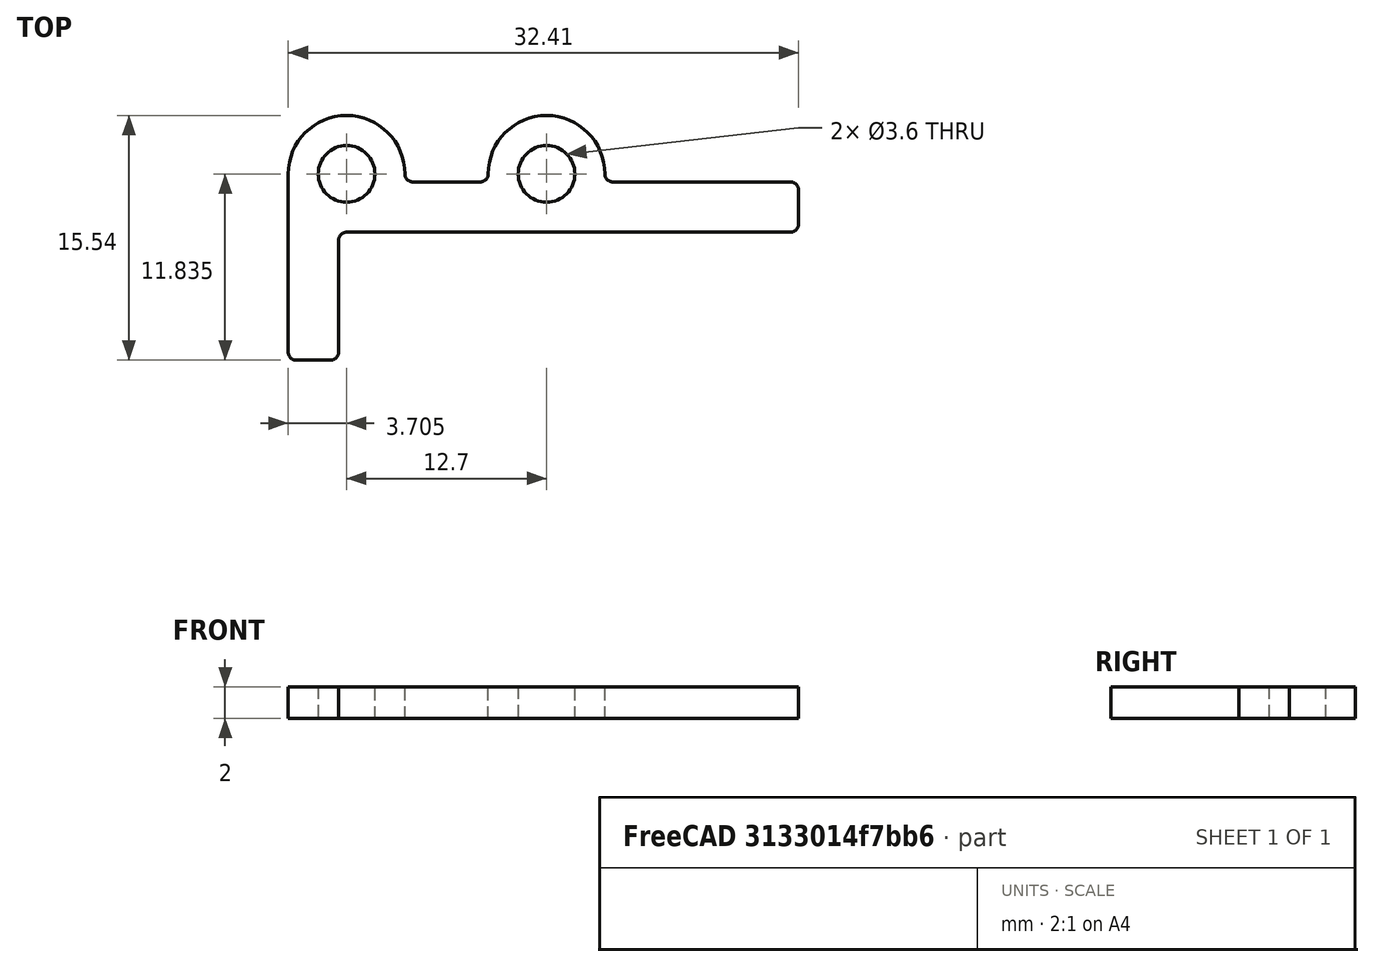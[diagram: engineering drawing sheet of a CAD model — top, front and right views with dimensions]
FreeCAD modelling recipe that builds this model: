
FCSTD DOCUMENT  (FreeCAD 0.22R38553 (Git))
Label: enclosure-panels
License: All rights reserved
LicenseURL: http://en.wikipedia.org/wiki/All_rights_reserved
objects: Sketcher::SketchObject×6, PartDesign::SubShapeBinder×1, PartDesign::Pad×1, PartDesign::Body×1
note: 17 computed .brp shape members not serialized (recipe doc carries the construction recipe); baked Part::Feature solids carry a one-line shape summary decoded from their .brp

FEATURE [Sketcher::SketchObject] Sketch  label="top"
  ArcFitTolerance = 1e-06
  FullyConstrained = true
  MakeInternals = false
  MapMode = 5
  expr: Constraints[23] = .Constraints.hole_distance
  sketch-geometry (14):
    g0: LineSegment StartX=-330.2 StartY=330.2 StartZ=0 EndX=-330.2 EndY=-330.2 EndZ=0
    g1: LineSegment StartX=-330.2 StartY=-330.2 StartZ=0 EndX=330.2 EndY=-330.2 EndZ=0
    g2: LineSegment StartX=330.2 StartY=-330.2 StartZ=0 EndX=330.2 EndY=330.2 EndZ=0
    g3: LineSegment StartX=330.2 StartY=330.2 StartZ=0 EndX=-330.2 EndY=330.2 EndZ=0
    g4: Circle CenterX=-292.1 CenterY=165.1 CenterZ=0 NormalX=0 NormalY=0 NormalZ=1 AngleXU=0 Radius=3.683
    g5: Circle CenterX=-292.1 CenterY=0 CenterZ=0 NormalX=0 NormalY=0 NormalZ=1 AngleXU=0 Radius=3.683
    g6: Circle CenterX=-292.1 CenterY=-165.1 CenterZ=0 NormalX=0 NormalY=0 NormalZ=1 AngleXU=0 Radius=3.683
    g7: Circle CenterX=292.1 CenterY=165.1 CenterZ=0 NormalX=0 NormalY=0 NormalZ=1 AngleXU=0 Radius=3.683
    g8: Circle CenterX=292.1 CenterY=0 CenterZ=0 NormalX=0 NormalY=0 NormalZ=1 AngleXU=0 Radius=3.683
    g9: Circle CenterX=292.1 CenterY=-165.1 CenterZ=0 NormalX=0 NormalY=0 NormalZ=1 AngleXU=0 Radius=3.683
    g10: LineSegment StartX=355.6 StartY=330.2 StartZ=0 EndX=355.6 EndY=320.2 EndZ=0
    g11: LineSegment StartX=355.6 StartY=320.2 StartZ=0 EndX=365.6 EndY=320.2 EndZ=0
    g12: LineSegment StartX=365.6 StartY=320.2 StartZ=0 EndX=365.6 EndY=330.2 EndZ=0
    g13: LineSegment StartX=365.6 StartY=330.2 StartZ=0 EndX=355.6 EndY=330.2 EndZ=0
  constraints (39):
    c: Coincident(g0,g1)
    c: Coincident(g1,g2)
    c: Coincident(g2,g3)
    c: Coincident(g3,g0)
    c: Vertical(g0)
    c: Vertical(g2)
    c: Horizontal(g1)
    c: Horizontal(g3)
    c: DistanceX(g3,g3) = 660.4
    c: DistanceY(g0,g0) = 660.4
    c: Symmetric(g0,g1,g-1)
    c: Diameter(g4) = 7.366
    c: DistanceX(g0,g4) = 38.1  'hole_distance'
    c: PointOnObject(g5,g-1)
    c: Equal(g4,g5)
    c: Equal(g4,g6)
    c: Vertical(g4,g5)
    c: Symmetric(g4,g6,g5)
    c: DistanceY(g4,g0) = 165.1
    c: Diameter(g7) = 7.366
    c: Equal(g7,g8)
    c: Equal(g7,g9)
    c: Symmetric(g7,g9,g8)
    c: DistanceX(g7,g2) = 38.1
    c: PointOnObject(g8,g-1)
    c: Horizontal(g4,g7)
    c: Vertical(g7,g8)
    c: Coincident(g10,g11)
    c: Coincident(g11,g12)
    c: Coincident(g12,g13)
    c: Coincident(g13,g10)
    c: Vertical(g10)
    c: Vertical(g12)
    c: Horizontal(g11)
    c: Horizontal(g13)
    c: Equal(g13,g10)
    c: Horizontal(g2,g10)
    c: Distance(g13,g13) = 10
    c: DistanceX(g2,g10) = 25.4
FEATURE [Sketcher::SketchObject] Sketch001  label="side"
  ArcFitTolerance = 1e-06
  FullyConstrained = true
  MakeInternals = false
  MapMode = 5
  expr: Constraints[23] = .Constraints.hole_distance
  sketch-geometry (22):
    g0: LineSegment StartX=-330.2 StartY=330.2 StartZ=0 EndX=-330.2 EndY=-330.2 EndZ=0
    g1: LineSegment StartX=-330.2 StartY=-330.2 StartZ=0 EndX=330.2 EndY=-330.2 EndZ=0
    g2: LineSegment StartX=330.2 StartY=-330.2 StartZ=0 EndX=330.2 EndY=330.2 EndZ=0
    g3: LineSegment StartX=330.2 StartY=330.2 StartZ=0 EndX=-330.2 EndY=330.2 EndZ=0
    g4: Circle CenterX=-292.1 CenterY=165.1 CenterZ=0 NormalX=0 NormalY=0 NormalZ=1 AngleXU=0 Radius=3.683
    g5: Circle CenterX=-292.1 CenterY=0 CenterZ=0 NormalX=0 NormalY=0 NormalZ=1 AngleXU=0 Radius=3.683
    g6: Circle CenterX=-292.1 CenterY=-165.1 CenterZ=0 NormalX=0 NormalY=0 NormalZ=1 AngleXU=0 Radius=3.683
    g7: Circle CenterX=292.1 CenterY=165.1 CenterZ=0 NormalX=0 NormalY=0 NormalZ=1 AngleXU=0 Radius=3.683
    g8: Circle CenterX=292.1 CenterY=0 CenterZ=0 NormalX=0 NormalY=0 NormalZ=1 AngleXU=0 Radius=3.683
    g9: Circle CenterX=292.1 CenterY=-165.1 CenterZ=0 NormalX=0 NormalY=0 NormalZ=1 AngleXU=0 Radius=3.683
    g10: LineSegment StartX=355.6 StartY=330.2 StartZ=0 EndX=355.6 EndY=320.2 EndZ=0
    g11: LineSegment StartX=355.6 StartY=320.2 StartZ=0 EndX=365.6 EndY=320.2 EndZ=0
    g12: LineSegment StartX=365.6 StartY=320.2 StartZ=0 EndX=365.6 EndY=330.2 EndZ=0
    g13: LineSegment StartX=365.6 StartY=330.2 StartZ=0 EndX=355.6 EndY=330.2 EndZ=0
    g14: Circle CenterX=177.8 CenterY=177.8 CenterZ=0 NormalX=0 NormalY=0 NormalZ=1 AngleXU=0 Radius=42.375
    g15: Circle CenterX=177.8 CenterY=126.8 CenterZ=0 NormalX=0 NormalY=0 NormalZ=1 AngleXU=0 Radius=1.8034
    g16: Circle CenterX=221.967 CenterY=203.3 CenterZ=0 NormalX=0 NormalY=0 NormalZ=1 AngleXU=0 Radius=1.8034
    g17: Circle CenterX=133.633 CenterY=203.3 CenterZ=0 NormalX=0 NormalY=0 NormalZ=1 AngleXU=0 Radius=1.8034
    g18: LineSegment [constr] StartX=177.8 StartY=177.8 StartZ=0 EndX=177.8 EndY=126.8 EndZ=0
    g19: LineSegment [constr] StartX=177.8 StartY=177.8 StartZ=0 EndX=221.967 EndY=203.3 EndZ=0
    g20: LineSegment [constr] StartX=177.8 StartY=177.8 StartZ=0 EndX=133.633 EndY=203.3 EndZ=0
    g21: Circle CenterX=-177.8 CenterY=-1.89e-14 CenterZ=0 NormalX=0 NormalY=0 NormalZ=1 AngleXU=0 Radius=4.5085
  constraints (62):
    c: Coincident(g0,g1)
    c: Coincident(g1,g2)
    c: Coincident(g2,g3)
    c: Coincident(g3,g0)
    c: Vertical(g0)
    c: Vertical(g2)
    c: Horizontal(g1)
    c: Horizontal(g3)
    c: DistanceX(g3,g3) = 660.4
    c: DistanceY(g0,g0) = 660.4
    c: Symmetric(g0,g1,g-1)
    c: Diameter(g4) = 7.366
    c: DistanceX(g0,g4) = 38.1  'hole_distance'
    c: PointOnObject(g5,g-1)
    c: Equal(g4,g5)
    c: Equal(g4,g6)
    c: Vertical(g4,g5)
    c: Symmetric(g4,g6,g5)
    c: DistanceY(g4,g0) = 165.1
    c: Diameter(g7) = 7.366
    c: Equal(g7,g8)
    c: Equal(g7,g9)
    c: Symmetric(g7,g9,g8)
    c: DistanceX(g7,g2) = 38.1
    c: PointOnObject(g8,g-1)
    c: Horizontal(g4,g7)
    c: Vertical(g7,g8)
    c: Coincident(g10,g11)
    c: Coincident(g11,g12)
    c: Coincident(g12,g13)
    c: Coincident(g13,g10)
    c: Vertical(g10)
    c: Vertical(g12)
    c: Horizontal(g11)
    c: Horizontal(g13)
    c: Equal(g13,g10)
    c: Horizontal(g2,g10)
    c: Distance(g13,g13) = 10
    c: DistanceX(g2,g10) = 25.4
    c: Diameter(g14) = 84.75
    c: Diameter(g15) = 3.6068
    c: Vertical(g14,g15)
    c: Equal(g15,g16)
    c: Equal(g15,g17)
    c: Coincident(g18,g14)
    c: Coincident(g18,g15)
    c: Coincident(g19,g14)
    c: Coincident(g19,g16)
    c: Coincident(g20,g14)
    c: Coincident(g20,g17)
    c: Equal(g18,g19)
    c: Equal(g18,g20)
    c: Distance(g15,g16) = 88.3346
    c: DistanceY(g14,g2) = 152.4
    c: Distance(g14,g2) = 152.4
    c: Diameter(g21) = 9.017
    c: DistanceX(g0,g21) = 152.4
    c: DistanceY(g0,g21) = 330.2
    c: DistanceY(g18,g18) = 51
    c: Angle(g20,g18) = 2.0944
    c: Angle(g18,g19) = 2.0944
    c: Diameter(g14) = 84.75
FEATURE [Sketcher::SketchObject] Sketch002  label="back"
  ArcFitTolerance = 1e-06
  FullyConstrained = true
  MakeInternals = false
  MapMode = 5
  expr: Constraints[23] = .Constraints.hole_distance
  sketch-geometry (23):
    g0: LineSegment StartX=-330.2 StartY=330.2 StartZ=0 EndX=-330.2 EndY=-330.2 EndZ=0
    g1: LineSegment StartX=-330.2 StartY=-330.2 StartZ=0 EndX=330.2 EndY=-330.2 EndZ=0
    g2: LineSegment StartX=330.2 StartY=-330.2 StartZ=0 EndX=330.2 EndY=330.2 EndZ=0
    g3: LineSegment StartX=330.2 StartY=330.2 StartZ=0 EndX=-330.2 EndY=330.2 EndZ=0
    g4: Circle CenterX=-292.1 CenterY=165.1 CenterZ=0 NormalX=0 NormalY=0 NormalZ=1 AngleXU=0 Radius=3.683
    g5: Circle CenterX=-292.1 CenterY=0 CenterZ=0 NormalX=0 NormalY=0 NormalZ=1 AngleXU=0 Radius=3.683
    g6: Circle CenterX=-292.1 CenterY=-165.1 CenterZ=0 NormalX=0 NormalY=0 NormalZ=1 AngleXU=0 Radius=3.683
    g7: Circle CenterX=292.1 CenterY=165.1 CenterZ=0 NormalX=0 NormalY=0 NormalZ=1 AngleXU=0 Radius=3.683
    g8: Circle CenterX=292.1 CenterY=0 CenterZ=0 NormalX=0 NormalY=0 NormalZ=1 AngleXU=0 Radius=3.683
    g9: Circle CenterX=292.1 CenterY=-165.1 CenterZ=0 NormalX=0 NormalY=0 NormalZ=1 AngleXU=0 Radius=3.683
    g10: LineSegment StartX=355.6 StartY=330.2 StartZ=0 EndX=355.6 EndY=320.2 EndZ=0
    g11: LineSegment StartX=355.6 StartY=320.2 StartZ=0 EndX=365.6 EndY=320.2 EndZ=0
    g12: LineSegment StartX=365.6 StartY=320.2 StartZ=0 EndX=365.6 EndY=330.2 EndZ=0
    g13: LineSegment StartX=365.6 StartY=330.2 StartZ=0 EndX=355.6 EndY=330.2 EndZ=0
    g14: Circle CenterX=-127 CenterY=-264.873 CenterZ=0 NormalX=0 NormalY=0 NormalZ=1 AngleXU=0 Radius=14.5274
    g15: Circle CenterX=-143 CenterY=-248.873 CenterZ=0 NormalX=0 NormalY=0 NormalZ=1 AngleXU=0 Radius=1.75
    g16: Circle CenterX=-111 CenterY=-248.873 CenterZ=0 NormalX=0 NormalY=0 NormalZ=1 AngleXU=0 Radius=1.75
    g17: Circle CenterX=-143 CenterY=-280.873 CenterZ=0 NormalX=0 NormalY=0 NormalZ=1 AngleXU=0 Radius=1.75
    g18: Circle CenterX=-111 CenterY=-280.873 CenterZ=0 NormalX=0 NormalY=0 NormalZ=1 AngleXU=0 Radius=1.75
    g19: LineSegment [constr] StartX=-127 StartY=-264.873 StartZ=0 EndX=-127 EndY=-279.4 EndZ=0
    g20: LineSegment [constr] StartX=-127 StartY=-264.873 StartZ=0 EndX=-111 EndY=-248.873 EndZ=0
    g21: GeomPoint [constr] X=-116.728 Y=-254.6 Z=0
    g22: GeomPoint [constr] X=-112.237 Y=-250.11 Z=0
  constraints (63):
    c: Coincident(g0,g1)
    c: Coincident(g1,g2)
    c: Coincident(g2,g3)
    c: Coincident(g3,g0)
    c: Vertical(g0)
    c: Vertical(g2)
    c: Horizontal(g1)
    c: Horizontal(g3)
    c: DistanceX(g3,g3) = 660.4
    c: DistanceY(g0,g0) = 660.4
    c: Symmetric(g0,g1,g-1)
    c: Diameter(g4) = 7.366
    c: DistanceX(g0,g4) = 38.1  'hole_distance'
    c: PointOnObject(g5,g-1)
    c: Equal(g4,g5)
    c: Equal(g4,g6)
    c: Vertical(g4,g5)
    c: Symmetric(g4,g6,g5)
    c: DistanceY(g4,g0) = 165.1
    c: Diameter(g7) = 7.366
    c: Equal(g7,g8)
    c: Equal(g7,g9)
    c: Symmetric(g7,g9,g8)
    c: DistanceX(g7,g2) = 38.1
    c: PointOnObject(g8,g-1)
    c: Horizontal(g4,g7)
    c: Vertical(g7,g8)
    c: Coincident(g10,g11)
    c: Coincident(g11,g12)
    c: Coincident(g12,g13)
    c: Coincident(g13,g10)
    c: Vertical(g10)
    c: Vertical(g12)
    c: Horizontal(g11)
    c: Horizontal(g13)
    c: Equal(g13,g10)
    c: Horizontal(g2,g10)
    c: Distance(g13,g13) = 10
    c: DistanceX(g2,g10) = 25.4
    c: Equal(g15,g16)
    c: Equal(g15,g17)
    c: Equal(g15,g18)
    c: DistanceY(g17,g15) = 31.9999
    c: DistanceX(g15,g16) = 31.9999
    c: Vertical(g15,g17)
    c: Vertical(g16,g18)
    c: Horizontal(g15,g16)
    c: Horizontal(g17,g18)
    c: Diameter(g15) = 3.49999
    c: Symmetric(g15,g18,g14)
    c: Coincident(g19,g14)
    c: PointOnObject(g19,g14)
    c: Vertical(g19)
    c: DistanceY(g0,g19) = 50.8
    c: DistanceX(g0,g14) = 203.2
    c: Coincident(g20,g14)
    c: Coincident(g20,g16)
    c: PointOnObject(g21,g14)
    c: PointOnObject(g21,g20)
    c: PointOnObject(g22,g16)
    c: PointOnObject(g22,g20)
    c: Distance(g21,g22) = 6.35
    c: Diameter(g14) = 29.0548
FEATURE [Sketcher::SketchObject] Sketch003  label="bottom"
  ArcFitTolerance = 1e-06
  FullyConstrained = true
  MakeInternals = false
  MapMode = 5
  expr: Constraints[66] = 1.53 "
  sketch-geometry (24):
    g0: LineSegment StartX=-328.93 StartY=271.526 StartZ=0 EndX=-328.93 EndY=-284.988 EndZ=0
    g1: LineSegment StartX=-302.768 StartY=-323.85 StartZ=0 EndX=302.768 EndY=-323.85 EndZ=0
    g2: LineSegment StartX=328.93 StartY=-284.988 StartZ=0 EndX=328.93 EndY=271.526 EndZ=0
    g3: LineSegment StartX=276.606 StartY=323.85 StartZ=0 EndX=-276.606 EndY=323.85 EndZ=0
    g4: LineSegment StartX=354.33 StartY=323.85 StartZ=0 EndX=354.33 EndY=313.85 EndZ=0
    g5: LineSegment StartX=354.33 StartY=313.85 StartZ=0 EndX=364.33 EndY=313.85 EndZ=0
    g6: LineSegment StartX=364.33 StartY=313.85 StartZ=0 EndX=364.33 EndY=323.85 EndZ=0
    g7: LineSegment StartX=364.33 StartY=323.85 StartZ=0 EndX=354.33 EndY=323.85 EndZ=0
    g8: GeomPoint [constr] X=-328.93 Y=323.85 Z=0
    g9: GeomPoint [constr] X=-328.93 Y=-323.85 Z=0
    g10: GeomPoint [constr] X=328.93 Y=-323.85 Z=0
    g11: GeomPoint [constr] X=328.93 Y=323.85 Z=0
    g12: LineSegment StartX=-328.93 StartY=271.526 StartZ=0 EndX=-302.768 EndY=271.526 EndZ=0
    g13: LineSegment StartX=-302.768 StartY=271.526 StartZ=0 EndX=-302.768 EndY=297.688 EndZ=0
    g14: LineSegment StartX=-302.768 StartY=297.688 StartZ=0 EndX=-276.606 EndY=297.688 EndZ=0
    g15: LineSegment StartX=-276.606 StartY=297.688 StartZ=0 EndX=-276.606 EndY=323.85 EndZ=0
    g16: LineSegment StartX=276.606 StartY=323.85 StartZ=0 EndX=276.606 EndY=297.688 EndZ=0
    g17: LineSegment StartX=276.606 StartY=297.688 StartZ=0 EndX=302.768 EndY=297.688 EndZ=0
    g18: LineSegment StartX=302.768 StartY=297.688 StartZ=0 EndX=302.768 EndY=271.526 EndZ=0
    g19: LineSegment StartX=302.768 StartY=271.526 StartZ=0 EndX=328.93 EndY=271.526 EndZ=0
    g20: LineSegment StartX=-328.93 StartY=-284.988 StartZ=0 EndX=-302.768 EndY=-284.988 EndZ=0
    g21: LineSegment StartX=-302.768 StartY=-284.988 StartZ=0 EndX=-302.768 EndY=-323.85 EndZ=0
    g22: LineSegment StartX=302.768 StartY=-323.85 StartZ=0 EndX=302.768 EndY=-284.988 EndZ=0
    g23: LineSegment StartX=302.768 StartY=-284.988 StartZ=0 EndX=328.93 EndY=-284.988 EndZ=0
  constraints (64):
    c: Vertical(g0)
    c: Vertical(g2)
    c: Horizontal(g1)
    c: Horizontal(g3)
    c: DistanceX(g8,g11) = 657.86
    c: DistanceY(g9,g8) = 647.7
    c: Symmetric(g8,g10,g-1)
    c: Coincident(g4,g5)
    c: Coincident(g5,g6)
    c: Coincident(g6,g7)
    c: Coincident(g7,g4)
    c: Vertical(g4)
    c: Vertical(g6)
    c: Horizontal(g5)
    c: Horizontal(g7)
    c: Equal(g7,g4)
    c: Horizontal(g11,g4)
    c: Distance(g7,g7) = 10
    c: DistanceX(g11,g4) = 25.4
    c: PointOnObject(g8,g0)
    c: PointOnObject(g8,g3)
    c: PointOnObject(g9,g0)
    c: PointOnObject(g9,g1)
    c: PointOnObject(g10,g1)
    c: PointOnObject(g10,g2)
    c: PointOnObject(g11,g2)
    c: PointOnObject(g11,g3)
    c: Coincident(g12,g0)
    c: Horizontal(g12)
    c: Coincident(g13,g12)
    c: Vertical(g13)
    c: Coincident(g14,g13)
    c: Horizontal(g14)
    c: Coincident(g15,g14)
    c: Coincident(g15,g3)
    c: Vertical(g15)
    c: Coincident(g3,g16)
    c: Coincident(g16,g17)
    c: Horizontal(g17)
    c: Coincident(g17,g18)
    c: Vertical(g18)
    c: Coincident(g18,g19)
    c: Coincident(g19,g2)
    c: Horizontal(g19)
    c: Vertical(g16)
    c: Equal(g12, g13-g16) x4
    c: Equal(g16,g17)
    c: Equal(g17,g18)
    c: Equal(g18,g19)
    c: Coincident(g0,g20)
    c: Horizontal(g20)
    c: Coincident(g20,g21)
    c: Coincident(g21,g1)
    c: Vertical(g21)
    c: Coincident(g1,g22)
    c: Vertical(g22)
    c: Coincident(g22,g23)
    c: Coincident(g23,g2)
    c: Horizontal(g23)
    c: Equal(g21,g22)
    c: Equal(g12,g20)
    c: Equal(g19,g23)
    c: Distance(g12,g12) = 26.162  'bracket_width'
    c: Distance(g21,g21) = 38.862
FEATURE [Sketcher::SketchObject] Sketch004  label="door"
  ArcFitTolerance = 1e-06
  FullyConstrained = true
  MakeInternals = false
  MapMode = 5
  expr: Constraints[36] = .Constraints.hinge_dist
  expr: Constraints[58] = .Constraints.door_stop_gap
  expr: Constraints[94] = .Constraints.door_stop_gap
  expr: Constraints[95] = .Constraints.door_stop_gap
  sketch-geometry (36):
    g0: LineSegment StartX=-151.765 StartY=304.038 StartZ=0 EndX=-151.765 EndY=-304.038 EndZ=0
    g1: LineSegment StartX=-151.765 StartY=-304.038 StartZ=0 EndX=151.765 EndY=-304.038 EndZ=0
    g2: LineSegment StartX=151.765 StartY=-304.038 StartZ=0 EndX=151.765 EndY=304.038 EndZ=0
    g3: LineSegment StartX=151.765 StartY=304.038 StartZ=0 EndX=-151.765 EndY=304.038 EndZ=0
    g4: LineSegment StartX=177.165 StartY=304.038 StartZ=0 EndX=177.165 EndY=314.038 EndZ=0
    g5: LineSegment StartX=177.165 StartY=314.038 StartZ=0 EndX=187.165 EndY=314.038 EndZ=0
    g6: LineSegment StartX=187.165 StartY=314.038 StartZ=0 EndX=187.165 EndY=304.038 EndZ=0
    g7: LineSegment StartX=187.165 StartY=304.038 StartZ=0 EndX=177.165 EndY=304.038 EndZ=0
    g8: Circle CenterX=107.823 CenterY=59.5 CenterZ=0 NormalX=0 NormalY=0 NormalZ=1 AngleXU=0 Radius=4.2545
    g9: Circle CenterX=107.823 CenterY=-59.5 CenterZ=0 NormalX=0 NormalY=0 NormalZ=1 AngleXU=0 Radius=4.2545
    g10: Circle CenterX=-135.255 CenterY=227.838 CenterZ=0 NormalX=0 NormalY=0 NormalZ=1 AngleXU=0 Radius=3.3782
    g11: Circle CenterX=-135.255 CenterY=199.847 CenterZ=0 NormalX=0 NormalY=0 NormalZ=1 AngleXU=0 Radius=3.3782
    g12: Circle CenterX=-135.255 CenterY=-199.847 CenterZ=0 NormalX=0 NormalY=0 NormalZ=1 AngleXU=0 Radius=3.3782
    g13: Circle CenterX=-135.255 CenterY=-227.838 CenterZ=0 NormalX=0 NormalY=0 NormalZ=1 AngleXU=0 Radius=3.3782
    g14: LineSegment [constr] StartX=-135.255 StartY=199.847 StartZ=0 EndX=-135.255 EndY=0 EndZ=0
    g15: LineSegment [constr] StartX=-135.255 StartY=-199.847 StartZ=0 EndX=-135.255 EndY=0 EndZ=0
    g16: LineSegment [constr] StartX=121.795 StartY=-302.768 StartZ=0 EndX=150.495 EndY=-302.768 EndZ=0
    g17: LineSegment [constr] StartX=150.495 StartY=-302.768 StartZ=0 EndX=150.495 EndY=-283.168 EndZ=0
    g18: LineSegment [constr] StartX=150.495 StartY=-283.168 StartZ=0 EndX=121.795 EndY=-283.168 EndZ=0
    g19: LineSegment [constr] StartX=121.795 StartY=-283.168 StartZ=0 EndX=121.795 EndY=-302.768 EndZ=0
    g20: Circle CenterX=136.145 CenterY=-292.968 CenterZ=0 NormalX=0 NormalY=0 NormalZ=1 AngleXU=0 Radius=2.75
    g21: Circle CenterX=134.495 CenterY=-278.955 CenterZ=0 NormalX=0 NormalY=0 NormalZ=1 AngleXU=0 Radius=1.8
    g22: Circle CenterX=121.795 CenterY=-278.955 CenterZ=0 NormalX=0 NormalY=0 NormalZ=1 AngleXU=0 Radius=1.8
    g23: LineSegment [constr] StartX=134.495 StartY=-278.955 StartZ=0 EndX=134.495 EndY=-280.755 EndZ=0
    g24: LineSegment [constr] StartX=134.495 StartY=-280.755 StartZ=0 EndX=134.495 EndY=-283.168 EndZ=0
    g25: LineSegment [constr] StartX=134.495 StartY=-278.955 StartZ=0 EndX=136.295 EndY=-278.955 EndZ=0
    g26: LineSegment [constr] StartX=121.795 StartY=302.768 StartZ=0 EndX=150.495 EndY=302.768 EndZ=0
    g27: LineSegment [constr] StartX=150.495 StartY=302.768 StartZ=0 EndX=150.495 EndY=283.168 EndZ=0
    g28: LineSegment [constr] StartX=150.495 StartY=283.168 StartZ=0 EndX=121.795 EndY=283.168 EndZ=0
    g29: LineSegment [constr] StartX=121.795 StartY=283.168 StartZ=0 EndX=121.795 EndY=302.768 EndZ=0
    g30: Circle CenterX=136.145 CenterY=292.968 CenterZ=0 NormalX=0 NormalY=0 NormalZ=1 AngleXU=0 Radius=2.75
    g31: Circle CenterX=134.495 CenterY=278.955 CenterZ=0 NormalX=0 NormalY=0 NormalZ=1 AngleXU=0 Radius=1.8
    g32: Circle CenterX=121.795 CenterY=278.955 CenterZ=0 NormalX=0 NormalY=0 NormalZ=1 AngleXU=0 Radius=1.8
    g33: LineSegment [constr] StartX=134.495 StartY=278.955 StartZ=0 EndX=134.495 EndY=280.755 EndZ=0
    g34: LineSegment [constr] StartX=134.495 StartY=280.755 StartZ=0 EndX=134.495 EndY=283.168 EndZ=0
    g35: LineSegment [constr] StartX=134.495 StartY=278.955 StartZ=0 EndX=136.295 EndY=278.955 EndZ=0
  constraints (103):
    c: Coincident(g0,g1)
    c: Coincident(g1,g2)
    c: Coincident(g2,g3)
    c: Coincident(g3,g0)
    c: Vertical(g0)
    c: Vertical(g2)
    c: Horizontal(g1)
    c: Horizontal(g3)
    c: DistanceX(g3,g3) = 303.53
    c: DistanceY(g0,g0) = 608.076
    c: Symmetric(g0,g1,g-1)
    c: Coincident(g4,g5)
    c: Coincident(g5,g6)
    c: Coincident(g6,g7)
    c: Coincident(g7,g4)
    c: Vertical(g4)
    c: Vertical(g6)
    c: Horizontal(g5)
    c: Horizontal(g7)
    c: Equal(g7,g4)
    c: Horizontal(g2,g4)
    c: Distance(g7,g7) = 10
    c: DistanceX(g2,g4) = 25.4
    c: Equal(g8,g9)
    c: Diameter(g8) = 8.509
    c: DistanceY(g9,g8) = 119
    c: Symmetric(g8,g9,g-1)
    c: DistanceX(g9,g1) = 43.942
    c: Equal(g10,g11)
    c: Equal(g10,g12)
    c: Equal(g10,g13)
    c: Diameter(g10) = 6.7564
    c: Vertical(g10,g11)
    c: Vertical(g10,g12)
    c: Vertical(g12,g13)
    c: DistanceY(g11,g10) = 27.9908  'hinge_dist'
    c: DistanceY(g13,g12) = 27.9908
    c: Coincident(g14,g11)
    c: PointOnObject(g14,g-1)
    c: Vertical(g14)
    c: Coincident(g15,g12)
    c: Coincident(g15,g14)
    c: Equal(g14,g15)
    c: DistanceX(g0,g10) = 16.51
    c: DistanceY(g10,g0) = 76.2
    c: Coincident(g16,g17)
    c: Coincident(g17,g18)
    c: Coincident(g18,g19)
    c: Coincident(g19,g16)
    c: Horizontal(g16)
    c: Horizontal(g18)
    c: Vertical(g17)
    c: Vertical(g19)
    c: DistanceX(g18,g18) = 28.7
    c: DistanceY(g19,g19) = 19.6
    c: Symmetric(g18,g16,g20)
    c: Diameter(g20) = 5.5
    c: Distance(g16,g2) = 1.27  'door_stop_gap'
    c: Distance(g16,g1) = 1.27
    c: Equal(g21,g22)
    c: Diameter(g21) = 3.6
    c: Coincident(g23,g21)
    c: PointOnObject(g23,g21)
    c: Vertical(g23)
    c: Coincident(g24,g23)
    c: PointOnObject(g24,g18)
    c: Vertical(g24)
    c: DistanceY(g24,g24) = 2.413
    c: Horizontal(g22,g21)
    c: DistanceX(g22,g21) = 12.7
    c: Coincident(g25,g21)
    c: PointOnObject(g25,g21)
    c: Horizontal(g25)
    c: Coincident(g26,g27)
    c: Coincident(g27,g28)
    c: Coincident(g28,g29)
    c: Coincident(g29,g26)
    c: Horizontal(g26)
    c: Horizontal(g28)
    c: Vertical(g27)
    c: Vertical(g29)
    c: Symmetric(g28,g26,g30)
    c: Diameter(g30) = 5.5
    c: Equal(g31,g32)
    c: Diameter(g31) = 3.6
    c: Coincident(g33,g31)
    c: PointOnObject(g33,g31)
    c: Vertical(g33)
    c: Coincident(g34,g33)
    c: PointOnObject(g34,g28)
    c: Vertical(g34)
    c: Coincident(g35,g31)
    c: PointOnObject(g35,g31)
    c: Horizontal(g35)
    c: DistanceY(g26,g2) = 1.27
    c: DistanceX(g26,g2) = 1.27
    c: Equal(g26,g18)
    c: Equal(g19,g29)
    c: Horizontal(g32,g31)
    c: DistanceY(g34,g34) = 2.413
    c: Vertical(g31,g21)
    c: Vertical(g22,g18)
    c: Vertical(g32,g22)
FEATURE [PartDesign::SubShapeBinder] Binder
  BindCopyOnChange = 0
  BindMode = 0
  ClaimChildren = false
  Context = -> Body [Binder.]
  Fuse = false
  MakeFace = true
  OffsetFill = false
  OffsetIntersection = false
  OffsetJoinType = 0
  OffsetOpenResult = false
  PartialLoad = false
  Relative = true
  Support = -> [Sketch004]
  _Version = 2
FEATURE [Sketcher::SketchObject] Sketch005  label="stops"
  ArcFitTolerance = 1e-06
  ExternalGeometry = -> [Binder]
  FullyConstrained = true
  MakeInternals = false
  MapMode = 5
  sketch-geometry (27):
    g0: LineSegment [constr] StartX=121.795 StartY=-302.768 StartZ=0 EndX=150.495 EndY=-302.768 EndZ=0
    g1: LineSegment [constr] StartX=150.495 StartY=-302.768 StartZ=0 EndX=150.495 EndY=-283.168 EndZ=0
    g2: LineSegment [constr] StartX=150.495 StartY=-283.168 StartZ=0 EndX=121.795 EndY=-283.168 EndZ=0
    g3: LineSegment [constr] StartX=121.795 StartY=-283.168 StartZ=0 EndX=121.795 EndY=-302.768 EndZ=0
    g4: Circle CenterX=121.795 CenterY=-278.955 CenterZ=0 NormalX=0 NormalY=0 NormalZ=1 AngleXU=0 Radius=1.8
    g5: LineSegment StartX=121.287 StartY=-283.168 StartZ=0 EndX=121.287 EndY=-290.28 EndZ=0
    g6: LineSegment StartX=120.779 StartY=-290.788 StartZ=0 EndX=118.598 EndY=-290.788 EndZ=0
    g7: LineSegment StartX=118.09 StartY=-290.28 StartZ=0 EndX=118.09 EndY=-278.955 EndZ=0
    g8: ArcOfCircle CenterX=121.795 CenterY=-283.168 CenterZ=0 NormalX=0 NormalY=0 NormalZ=1 AngleXU=0 Radius=0.508 StartAngle=1.5708 EndAngle=3.14159
    g9: ArcOfCircle CenterX=121.795 CenterY=-278.955 CenterZ=0 NormalX=0 NormalY=0 NormalZ=1 AngleXU=0 Radius=3.705 StartAngle=4.1e-15 EndAngle=3.14159
    g10: ArcOfCircle CenterX=126.008 CenterY=-278.955 CenterZ=0 NormalX=0 NormalY=0 NormalZ=1 AngleXU=0 Radius=0.508 StartAngle=3.14159 EndAngle=4.71239
    g11: LineSegment StartX=126.008 StartY=-279.463 StartZ=0 EndX=130.282 EndY=-279.463 EndZ=0
    g12: ArcOfCircle CenterX=130.282 CenterY=-278.955 CenterZ=0 NormalX=0 NormalY=0 NormalZ=1 AngleXU=0 Radius=0.508 StartAngle=4.71239 EndAngle=6.28319
    g13: ArcOfCircle CenterX=118.598 CenterY=-290.28 CenterZ=0 NormalX=0 NormalY=0 NormalZ=1 AngleXU=0 Radius=0.508 StartAngle=3.14159 EndAngle=4.71239
    g14: GeomPoint [constr] X=118.09 Y=-290.788 Z=0
    g15: ArcOfCircle CenterX=120.779 CenterY=-290.28 CenterZ=0 NormalX=0 NormalY=0 NormalZ=1 AngleXU=0 Radius=0.508 StartAngle=4.71239 EndAngle=6.28319
    g16: GeomPoint [constr] X=121.287 Y=-290.788 Z=0
    g17: ArcOfCircle CenterX=149.987 CenterY=-282.152 CenterZ=0 NormalX=0 NormalY=0 NormalZ=1 AngleXU=0 Radius=0.508 StartAngle=4.71239 EndAngle=6.28319
    g18: Circle CenterX=134.495 CenterY=-278.955 CenterZ=0 NormalX=0 NormalY=0 NormalZ=1 AngleXU=0 Radius=1.8
    g19: ArcOfCircle CenterX=134.495 CenterY=-278.955 CenterZ=0 NormalX=0 NormalY=0 NormalZ=1 AngleXU=0 Radius=3.705 StartAngle=5.9e-15 EndAngle=3.14159
    g20: ArcOfCircle CenterX=138.708 CenterY=-278.955 CenterZ=0 NormalX=0 NormalY=0 NormalZ=1 AngleXU=0 Radius=0.508 StartAngle=3.14159 EndAngle=4.71239
    g21: LineSegment StartX=138.708 StartY=-279.463 StartZ=0 EndX=149.987 EndY=-279.463 EndZ=0
    g22: ArcOfCircle CenterX=149.987 CenterY=-279.971 CenterZ=0 NormalX=0 NormalY=0 NormalZ=1 AngleXU=0 Radius=0.508 StartAngle=4.06e-14 EndAngle=1.5708
    g23: LineSegment StartX=150.495 StartY=-282.152 StartZ=0 EndX=150.495 EndY=-279.971 EndZ=0
    g24: LineSegment [constr] StartX=134.495 StartY=-278.955 StartZ=0 EndX=136.295 EndY=-278.955 EndZ=0
    g25: LineSegment [constr] StartX=136.295 StartY=-278.955 StartZ=0 EndX=138.2 EndY=-278.955 EndZ=0
    g26: LineSegment StartX=121.795 StartY=-282.66 StartZ=0 EndX=149.987 EndY=-282.66 EndZ=0
  constraints (65):
    c: Coincident(g0,g1)
    c: Coincident(g1,g2)
    c: Coincident(g2,g3)
    c: Coincident(g3,g0)
    c: Horizontal(g0)
    c: Horizontal(g2)
    c: Vertical(g1)
    c: Vertical(g3)
    c: DistanceX(g2,g2) = 28.7
    c: DistanceY(g3,g3) = 19.6
    c: Diameter(g4) = 3.6
    c: Vertical(g5)
    c: Horizontal(g6)
    c: Vertical(g7)
    c: Tangent(g5,g8) = -1.5708
    c: Tangent(g7,g9) = 1.5708
    c: Tangent(g9,g10) = 1.5708
    c: Tangent(g10,g11) = -1.5708
    c: Tangent(g11,g12) = -1.5708
    c: Horizontal(g11)
    c: Equal(g10,g12)
    c: PointOnObject(g14,g7)
    c: PointOnObject(g14,g6)
    c: Tangent(g7,g13) = 1.5708
    c: Tangent(g6,g13) = 1.5708
    c: PointOnObject(g16,g6)
    c: PointOnObject(g16,g5)
    c: Tangent(g6,g15) = 1.5708
    c: Tangent(g5,g15) = 1.5708
    c: Equal(g10,g8)
    c: Equal(g10,g15)
    c: Equal(g10,g13)
    c: Horizontal(g10,g9)
    c: Coincident(g8,g2)
    c: DistanceY(g6,g2) = 7.62
    c: Symmetric(g2,g0,g-3)
    c: Coincident(g9,g4)
    c: Equal(g17,g12)
    c: Coincident(g4,g-5)
    c: Tangent(g12,g19) = 1.5708
    c: Tangent(g19,g20) = 1.5708
    c: Tangent(g20,g21) = -1.5708
    c: Tangent(g21,g22) = 1.5708
    c: Horizontal(g21)
    c: Tangent(g23,g22) = -1.5708
    c: Vertical(g23)
    c: Coincident(g19,g18)
    c: Horizontal(g11,g20)
    c: Equal(g12,g20)
    c: Coincident(g24,g18)
    c: PointOnObject(g24,g18)
    c: Horizontal(g24)
    c: Coincident(g25,g24)
    c: Coincident(g25,g19)
    c: DistanceX(g25,g25) = 1.905
    c: Equal(g-4,g18)
    c: Equal(g9,g19)
    c: Equal(g20,g22)
    c: Coincident(g18,g-4)
    c: Horizontal(g26)
    c: DistanceY(g1,g17) = 0.508
    c: Vertical(g17,g1)
    c: Tangent(g26,g8) = 1.5708
    c: Tangent(g26,g17) = -1.5708
    c: Tangent(g23,g17) = -1.5708
FEATURE [PartDesign::Pad] Pad
  Direction = (0,0,1)
  Length = 2
  Length2 = 10
  Profile = -> Sketch005
  ReferenceAxis = -> Sketch005 [N_Axis]
  Suppressed = false
  Type = 0
FEATURE [PartDesign::Body] Body  label="door_stops"
  AllowCompound = false
  Group = -> [Binder,Sketch005,Pad]
  Origin = -> Origin
  Tip = -> Pad
